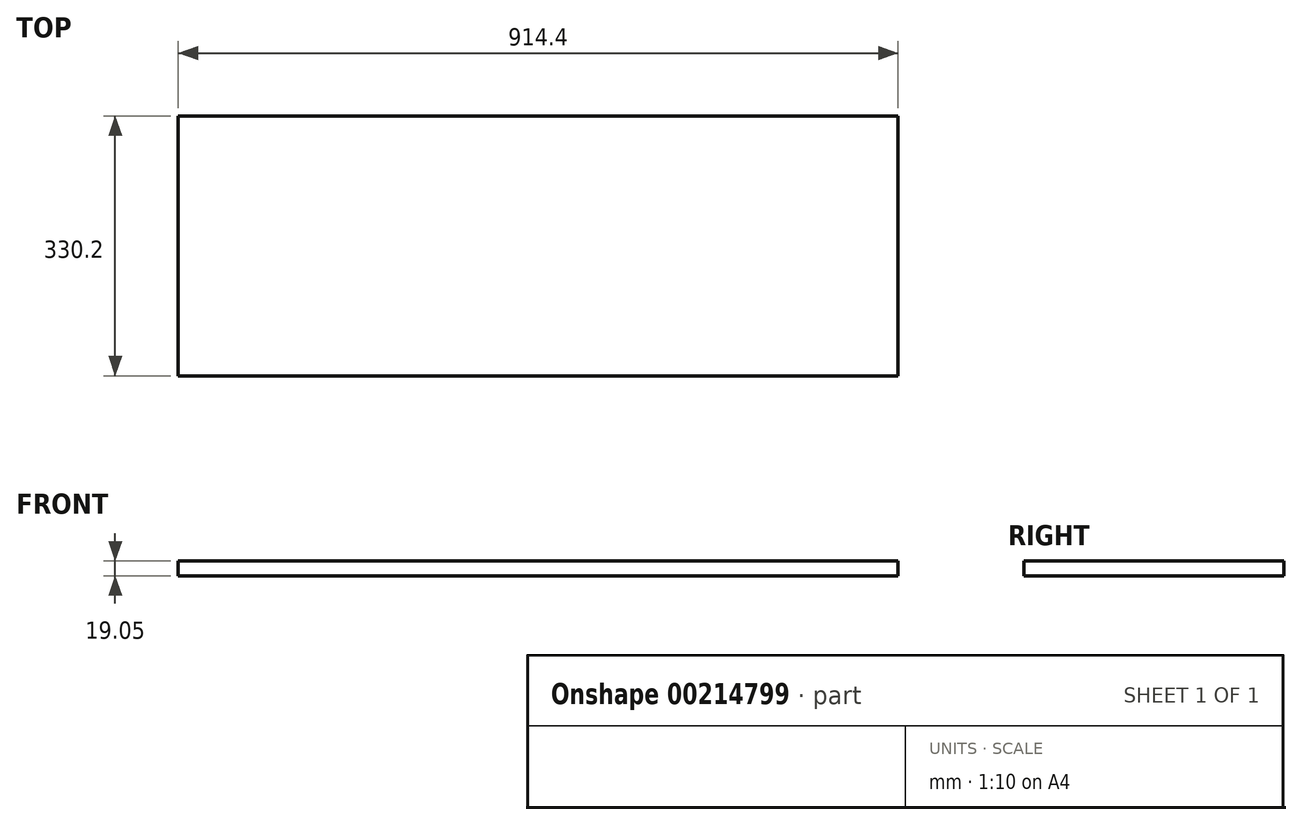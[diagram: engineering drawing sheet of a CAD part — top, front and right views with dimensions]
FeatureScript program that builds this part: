
annotation { "Feature Type Name" : "Feature", "Feature Type Description" : "" }
export const myFeature = defineFeature(function(context is Context, id is Id, definition is map)
    precondition{}
    {
        {
            var Q0;
            Q0=qCreatedBy(makeId("Top.planeOp"),FACE);
            var sketch = newSketch(context, id + "F0", { "sketchPlane" : qUnion([Q0])});
            skLineSegment(sketch, "E0.bottom", {"start": v(0, 0) * mm, "end": v(914.4, 0) * mm});
            skLineSegment(sketch, "E0.top", {"start": v(0, -330.2) * mm, "end": v(914.4, -330.2) * mm});
            skLineSegment(sketch, "E0.left", {"start": v(0, 0) * mm, "end": v(0, -330.2) * mm});
            skLineSegment(sketch, "E0.right", {"start": v(914.4, 0) * mm, "end": v(914.4, -330.2) * mm});
            skSolve(sketch);
        }
        {
            var Q0;
            Q0=makeQuery(id+"F0.imprint","IMPRINT",FACE,{"disambiguationData":[TD([[makeQuery(id+"F0.imprint","IMPRINT",EDGE,{"derivedFrom":sQuery(id+"F0.wireOp",EDGE,"E0.bottom")}),-1.0]])]});
            extrude(context, id + "F1", {"entities" : qUnion([Q0]), "depth" : 19.05 * mm});
        }
    });
